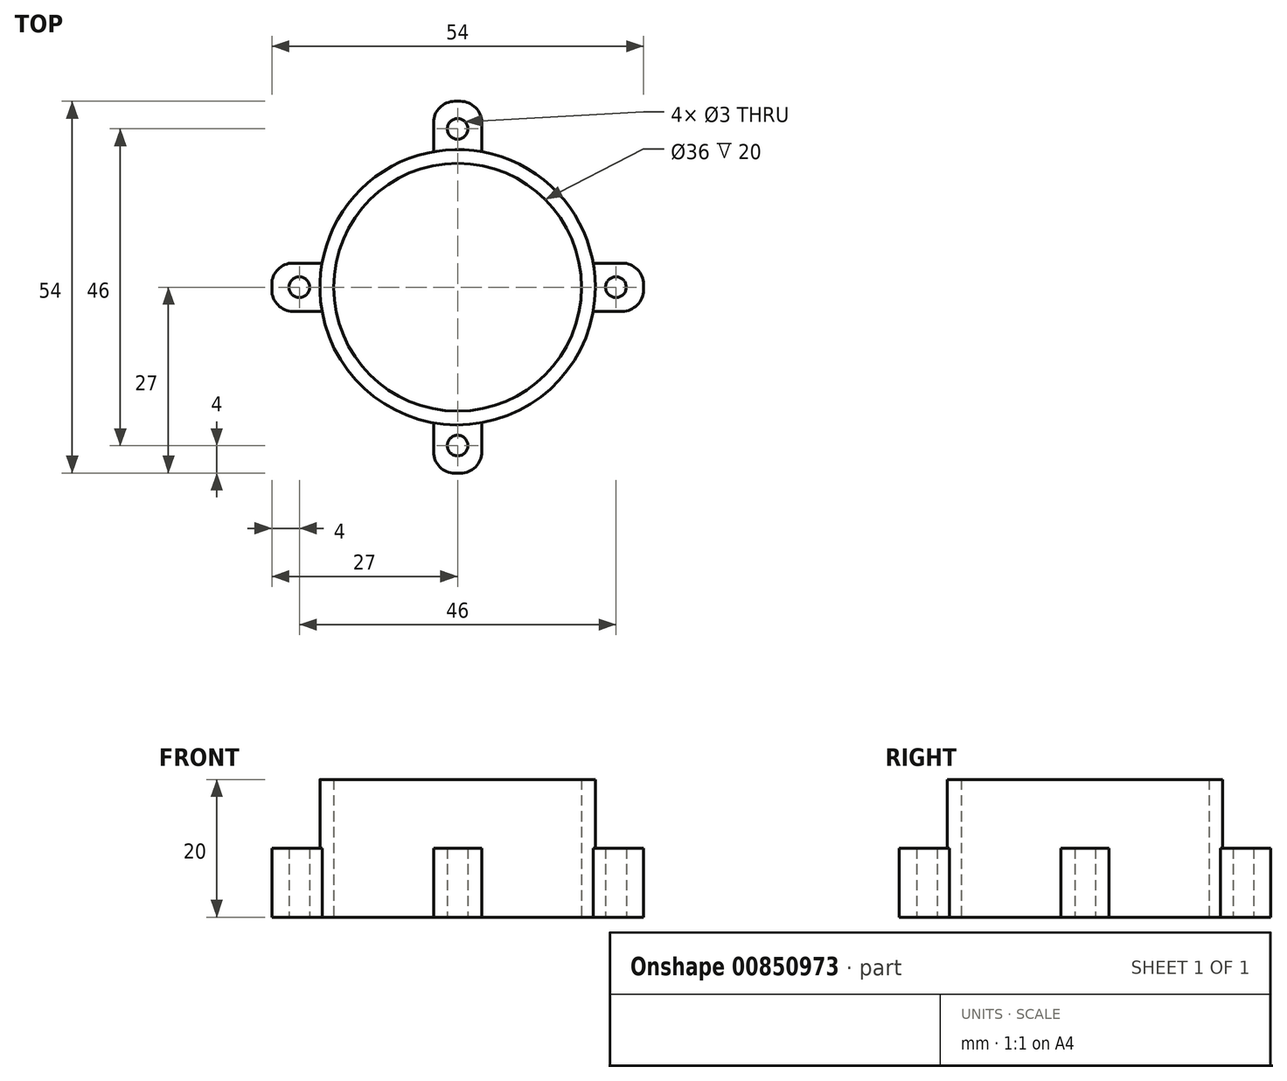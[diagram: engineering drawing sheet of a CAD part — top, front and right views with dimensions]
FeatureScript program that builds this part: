
annotation { "Feature Type Name" : "Feature", "Feature Type Description" : "" }
export const myFeature = defineFeature(function(context is Context, id is Id, definition is map)
    precondition{}
    {
        {
            var Q0;
            Q0=qCreatedBy(makeId("Top.planeOp"),FACE);
            var sketch = newSketch(context, id + "F0", { "sketchPlane" : qUnion([Q0])});
            skCircle(sketch, "E0", {"center": v(0, 0) * mm, "radius": 20 * mm});
            skLineSegment(sketch, "E1.bottom", {"start": v(-27, 3.5) * mm, "end": v(-13, 3.5) * mm});
            skLineSegment(sketch, "E1.top", {"start": v(-27, -3.5) * mm, "end": v(-13, -3.5) * mm});
            skLineSegment(sketch, "E1.left", {"start": v(-27, 3.5) * mm, "end": v(-27, -3.5) * mm});
            skPoint(sketch, "E1.middle", {"position": v(-20, 0) * mm});
            skLineSegment(sketch, "E2.1.0", {"start": v(-3.5, -27) * mm, "end": v(3.5, -27) * mm});
            skLineSegment(sketch, "E2.1.1", {"start": v(-3.5, -27) * mm, "end": v(-3.5, -13) * mm});
            skLineSegment(sketch, "E2.1.2", {"start": v(3.5, -27) * mm, "end": v(3.5, -13) * mm});
            skLineSegment(sketch, "E2.2.0", {"start": v(27, -3.5) * mm, "end": v(27, 3.5) * mm});
            skLineSegment(sketch, "E2.2.1", {"start": v(27, -3.5) * mm, "end": v(13, -3.5) * mm});
            skLineSegment(sketch, "E2.2.2", {"start": v(27, 3.5) * mm, "end": v(13, 3.5) * mm});
            skLineSegment(sketch, "E2.3.0", {"start": v(3.5, 27) * mm, "end": v(-3.5, 27) * mm});
            skLineSegment(sketch, "E2.3.1", {"start": v(3.5, 27) * mm, "end": v(3.5, 13) * mm});
            skLineSegment(sketch, "E2.3.2", {"start": v(-3.5, 27) * mm, "end": v(-3.5, 13) * mm});
            skPoint(sketch, "E3", {"position": v(23, 0) * mm});
            skPoint(sketch, "E4.1.0", {"position": v(0, 23) * mm});
            skPoint(sketch, "E4.2.0", {"position": v(-23, 0) * mm});
            skPoint(sketch, "E4.3.0", {"position": v(0, -23) * mm});
            skSolve(sketch);
        }
        {
            var Q0;
            {var subQ0=sQuery(id+"F0.wireOp",EDGE,"E0");var subQ4=makeQuery(id+"F0.imprint","INTERSECT",VERTEX,{"derivedFrom":[subQ0,sQuery(id+"F0.wireOp",EDGE,"E2.3.1")]});Q0=makeQuery(id+"F0.imprint","IMPRINT",FACE,{"disambiguationData":[TD([[makeQuery(id+"F0.imprint","IMPRINT",EDGE,{"disambiguationData":[TD([[subQ4,1.0]])],"derivedFrom":subQ0}),1.0]])]});}
            extrude(context, id + "F1", {"entities" : qUnion([Q0]), "depth" : 20 * mm, "offsetDistance" : 25 * mm});
        }
        {
            var Q0;
            Q0=makeQuery(id+"F1.opExtrude","CAP_FACE",FACE,{"disambiguationData":[OSD([sQuery(id+"F0.wireOp",EDGE,"E0")])],"isStart":false});
            var Q1;
            Q1=makeQuery(id+"F1.opExtrude","CAP_FACE",FACE,{"disambiguationData":[OSD([sQuery(id+"F0.wireOp",EDGE,"E0")])],"isStart":true});
            shell(context, id + "F2", {"entities" : qUnion([Q0, Q1]), "thickness" : 2 * mm});
        }
        {
            var Q0;
            {var subQ5=sQuery(id+"F0.wireOp",EDGE,"E1.left");Q0=makeQuery(id+"F0.imprint","IMPRINT",FACE,{"disambiguationData":[TD([[makeQuery(id+"F0.imprint","IMPRINT",EDGE,{"derivedFrom":subQ5}),1.0]])]});}
            var Q1;
            {var subQ5=sQuery(id+"F0.wireOp",EDGE,"E2.3.0");Q1=makeQuery(id+"F0.imprint","IMPRINT",FACE,{"disambiguationData":[TD([[makeQuery(id+"F0.imprint","IMPRINT",EDGE,{"derivedFrom":subQ5}),1.0]])]});}
            var Q2;
            {var subQ5=sQuery(id+"F0.wireOp",EDGE,"E2.2.0");Q2=makeQuery(id+"F0.imprint","IMPRINT",FACE,{"disambiguationData":[TD([[makeQuery(id+"F0.imprint","IMPRINT",EDGE,{"derivedFrom":subQ5}),1.0]])]});}
            var Q3;
            {var subQ5=sQuery(id+"F0.wireOp",EDGE,"E2.1.0");Q3=makeQuery(id+"F0.imprint","IMPRINT",FACE,{"disambiguationData":[TD([[makeQuery(id+"F0.imprint","IMPRINT",EDGE,{"derivedFrom":subQ5}),1.0]])]});}
            extrude(context, id + "F3", {"entities" : qUnion([Q0, Q1, Q2, Q3]), "operationType" : NewBodyOperationType.ADD, "depth" : 10 * mm, "offsetDistance" : 25 * mm});
        }
        {
            var Q0;
            Q0=makeQuery(id+"F3.opExtrude","SWEPT_EDGE",EDGE,{"disambiguationData":[OSD([sQuery(id+"F0.wireOp",EDGE,"E2.2.0"),sQuery(id+"F0.wireOp",EDGE,"E2.2.2")])]});
            var Q1;
            Q1=makeQuery(id+"F3.opExtrude","SWEPT_EDGE",EDGE,{"disambiguationData":[OSD([sQuery(id+"F0.wireOp",EDGE,"E2.2.0"),sQuery(id+"F0.wireOp",EDGE,"E2.2.1")])]});
            var Q2;
            Q2=makeQuery(id+"F3.opExtrude","SWEPT_EDGE",EDGE,{"disambiguationData":[OSD([sQuery(id+"F0.wireOp",EDGE,"E2.3.0"),sQuery(id+"F0.wireOp",EDGE,"E2.3.1")])]});
            var Q3;
            Q3=makeQuery(id+"F3.opExtrude","SWEPT_EDGE",EDGE,{"disambiguationData":[OSD([sQuery(id+"F0.wireOp",EDGE,"E2.1.0"),sQuery(id+"F0.wireOp",EDGE,"E2.1.2")])]});
            var Q4;
            Q4=makeQuery(id+"F3.opExtrude","SWEPT_EDGE",EDGE,{"disambiguationData":[OSD([sQuery(id+"F0.wireOp",EDGE,"E1.top"),sQuery(id+"F0.wireOp",EDGE,"E1.left")])]});
            var Q5;
            Q5=makeQuery(id+"F3.opExtrude","SWEPT_EDGE",EDGE,{"disambiguationData":[OSD([sQuery(id+"F0.wireOp",EDGE,"E2.1.0"),sQuery(id+"F0.wireOp",EDGE,"E2.1.1")])]});
            var Q6;
            Q6=makeQuery(id+"F3.opExtrude","SWEPT_EDGE",EDGE,{"disambiguationData":[OSD([sQuery(id+"F0.wireOp",EDGE,"E1.bottom"),sQuery(id+"F0.wireOp",EDGE,"E1.left")])]});
            var Q7;
            Q7=makeQuery(id+"F3.opExtrude","SWEPT_EDGE",EDGE,{"disambiguationData":[OSD([sQuery(id+"F0.wireOp",EDGE,"E2.3.0"),sQuery(id+"F0.wireOp",EDGE,"E2.3.2")])]});
            fillet(context, id + "F4", {"entities" : qUnion([Q0, Q1, Q2, Q3, Q4, Q5, Q6, Q7]), "radius" : 3.1 * mm, "tangentPropagation" : true, "allowEdgeOverflow" : false});
        }
        {
            var Q0;
            Q0=sQuery(id+"F0.wireOp",VERTEX,"E3");
            var Q1;
            Q1=sQuery(id+"F0.wireOp",VERTEX,"E4.3.0");
            var Q2;
            Q2=sQuery(id+"F0.wireOp",VERTEX,"E4.2.0");
            var Q3;
            Q3=sQuery(id+"F0.wireOp",VERTEX,"E4.1.0");
            var Q4;
            Q4=makeQuery(id+"F1.opExtrude","SWEPT_BODY",BODY,{"disambiguationData":[OSD([sQuery(id+"F0.wireOp",EDGE,"E0")])]});
            hole(context, id + "F5", {"style" : HoleStyle.SIMPLE, "endStyle" : HoleEndStyle.THROUGH, "oppositeDirection" : true, "holeDiameter" : 3 * mm, "majorDiameter" : 5 * mm, "isTappedThrough" : true, "tappedDepth" : 4 * mm, "tapClearance" : 3, "locations" : qUnion([Q0, Q1, Q2, Q3]), "scope" : qUnion([Q4])});
        }
    });
